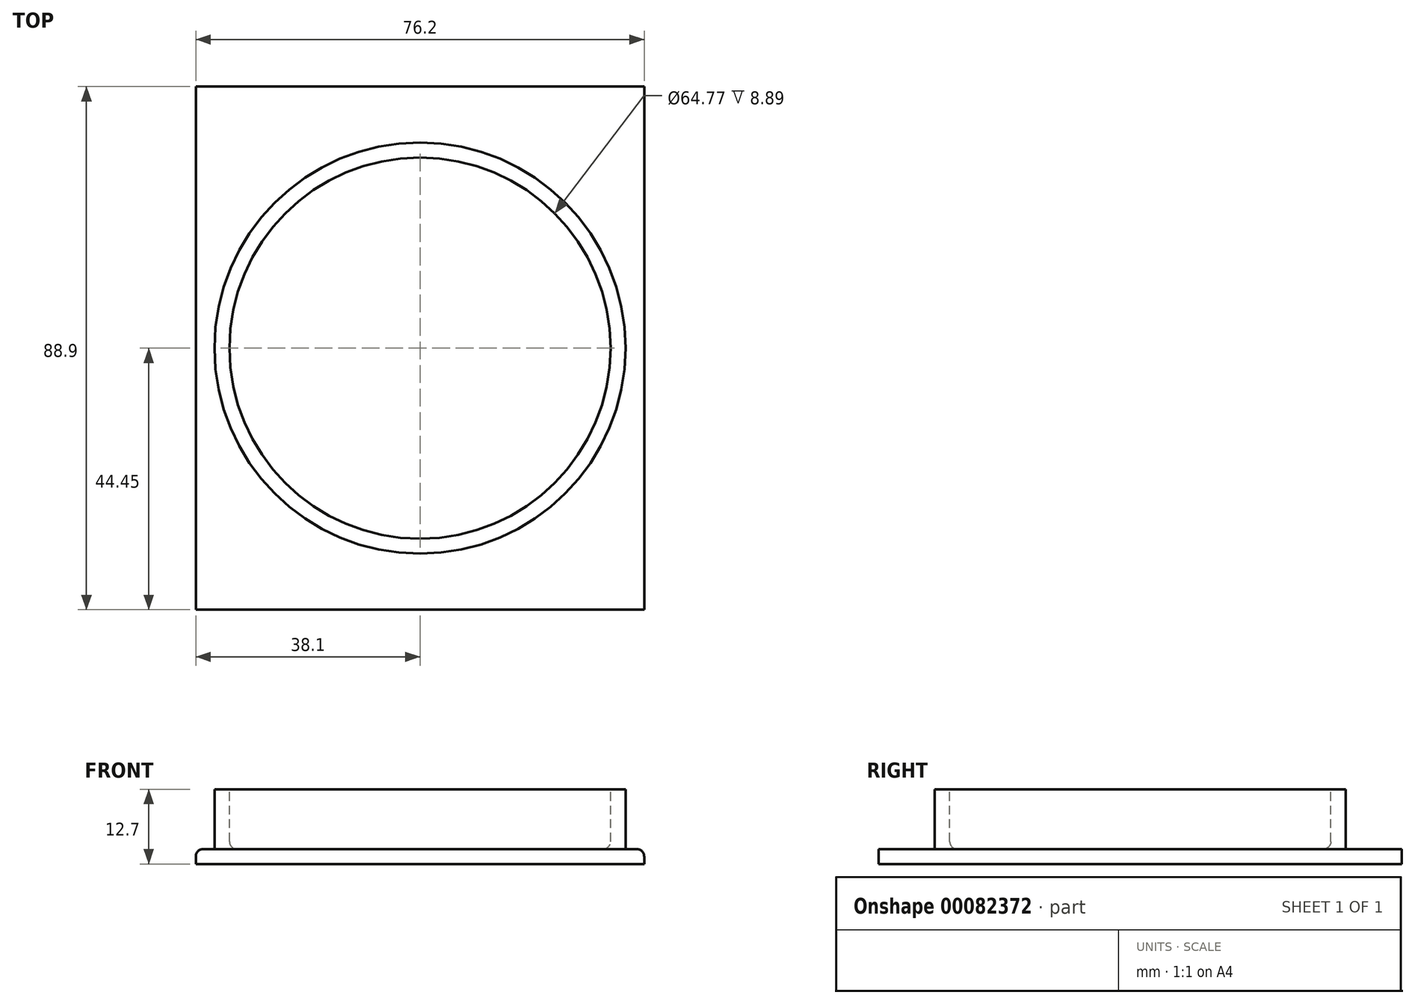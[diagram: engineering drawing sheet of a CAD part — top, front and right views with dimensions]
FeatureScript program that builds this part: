
annotation { "Feature Type Name" : "Feature", "Feature Type Description" : "" }
export const myFeature = defineFeature(function(context is Context, id is Id, definition is map)
    precondition{}
    {
        {
            var Q0;
            Q0=qCreatedBy(makeId("Top.planeOp"),FACE);
            var sketch = newSketch(context, id + "F0", { "sketchPlane" : qUnion([Q0])});
            skLineSegment(sketch, "E0.bottom", {"start": v(0, 0) * mm, "end": v(76.2, 0) * mm});
            skLineSegment(sketch, "E0.top", {"start": v(0, 88.9) * mm, "end": v(76.2, 88.9) * mm});
            skLineSegment(sketch, "E0.left", {"start": v(0, 0) * mm, "end": v(0, 88.9) * mm});
            skLineSegment(sketch, "E0.right", {"start": v(76.2, 0) * mm, "end": v(76.2, 88.9) * mm});
            skSolve(sketch);
        }
        {
            var Q0;
            Q0=makeQuery(id+"F0.imprint","IMPRINT",FACE,{"disambiguationData":[TD([[makeQuery(id+"F0.imprint","IMPRINT",EDGE,{"derivedFrom":sQuery(id+"F0.wireOp",EDGE,"E0.bottom")}),1.0]])]});
            extrude(context, id + "F1", {"entities" : qUnion([Q0]), "depth" : 2.54 * mm});
        }
        {
            var Q0;
            Q0=makeQuery(id+"F1.opExtrude","CAP_FACE",FACE,{"disambiguationData":[OSD([sQuery(id+"F0.wireOp",EDGE,"E0.bottom"),sQuery(id+"F0.wireOp",EDGE,"E0.top"),sQuery(id+"F0.wireOp",EDGE,"E0.left"),sQuery(id+"F0.wireOp",EDGE,"E0.right")])],"isStart":false});
            var sketch = newSketch(context, id + "F2", { "sketchPlane" : qUnion([Q0])});
            skLineSegment(sketch, "E1", {"start": v(38.1, 88.9) * mm, "end": v(38.1, 0) * mm, "construction": true});
            skLineSegment(sketch, "E2", {"start": v(0, 44.45) * mm, "end": v(76.2, 44.45) * mm, "construction": true});
            skCircle(sketch, "E3", {"center": v(38.1, 44.45) * mm, "radius": 34.93 * mm});
            skSolve(sketch);
        }
        {
            var Q0;
            Q0 = qSketchRegion(id + "F2", true);
            extrude(context, id + "F3", {"entities" : qUnion([Q0]), "operationType" : NewBodyOperationType.ADD, "depth" : 10.16 * mm});
        }
        {
            var Q0;
            Q0=makeQuery(id+"F3.opExtrude","CAP_FACE",FACE,{"disambiguationData":[OSD([sQuery(id+"F2.wireOp",EDGE,"E3")])],"isStart":false});
            var sketch = newSketch(context, id + "F4", { "sketchPlane" : qUnion([Q0])});
            skCircle(sketch, "E4", {"center": v(38.1, 44.45) * mm, "radius": 32.39 * mm});
            skSolve(sketch);
        }
        {
            var Q0;
            Q0=makeQuery(id+"F4.imprint","IMPRINT",FACE,{"disambiguationData":[TD([[makeQuery(id+"F4.imprint","IMPRINT",EDGE,{"derivedFrom":sQuery(id+"F4.wireOp",EDGE,"E4")}),1.0]])]});
            extrude(context, id + "F5", {"entities" : qUnion([Q0]), "operationType" : NewBodyOperationType.REMOVE, "oppositeDirection" : true, "depth" : 10.16 * mm});
        }
        {
            var Q0;
            Q0=makeQuery(id+"F5.boolean.opBoolean","COPY",EDGE,{"derivedFrom":makeQuery(id+"F5.opExtrude","CAP_EDGE",EDGE,{"disambiguationData":[OSD([sQuery(id+"F4.wireOp",EDGE,"E4")])],"isStart":false})});
            var Q1;
            Q1=makeQuery(id+"F1.opExtrude","CAP_EDGE",EDGE,{"disambiguationData":[OSD([sQuery(id+"F0.wireOp",EDGE,"E0.left")])],"isStart":false});
            var Q2;
            Q2=makeQuery(id+"F1.opExtrude","CAP_EDGE",EDGE,{"disambiguationData":[OSD([sQuery(id+"F0.wireOp",EDGE,"E0.right")])],"isStart":false});
            var Q3;
            Q3=makeQuery(id+"F3.opExtrude","CAP_EDGE",EDGE,{"disambiguationData":[OSD([sQuery(id+"F2.wireOp",EDGE,"E3")])],"isStart":true});
            fillet(context, id + "F6", {"entities" : qUnion([Q0, Q1, Q2, Q3]), "radius" : 1.27 * mm, "allowEdgeOverflow" : false});
        }
    });
